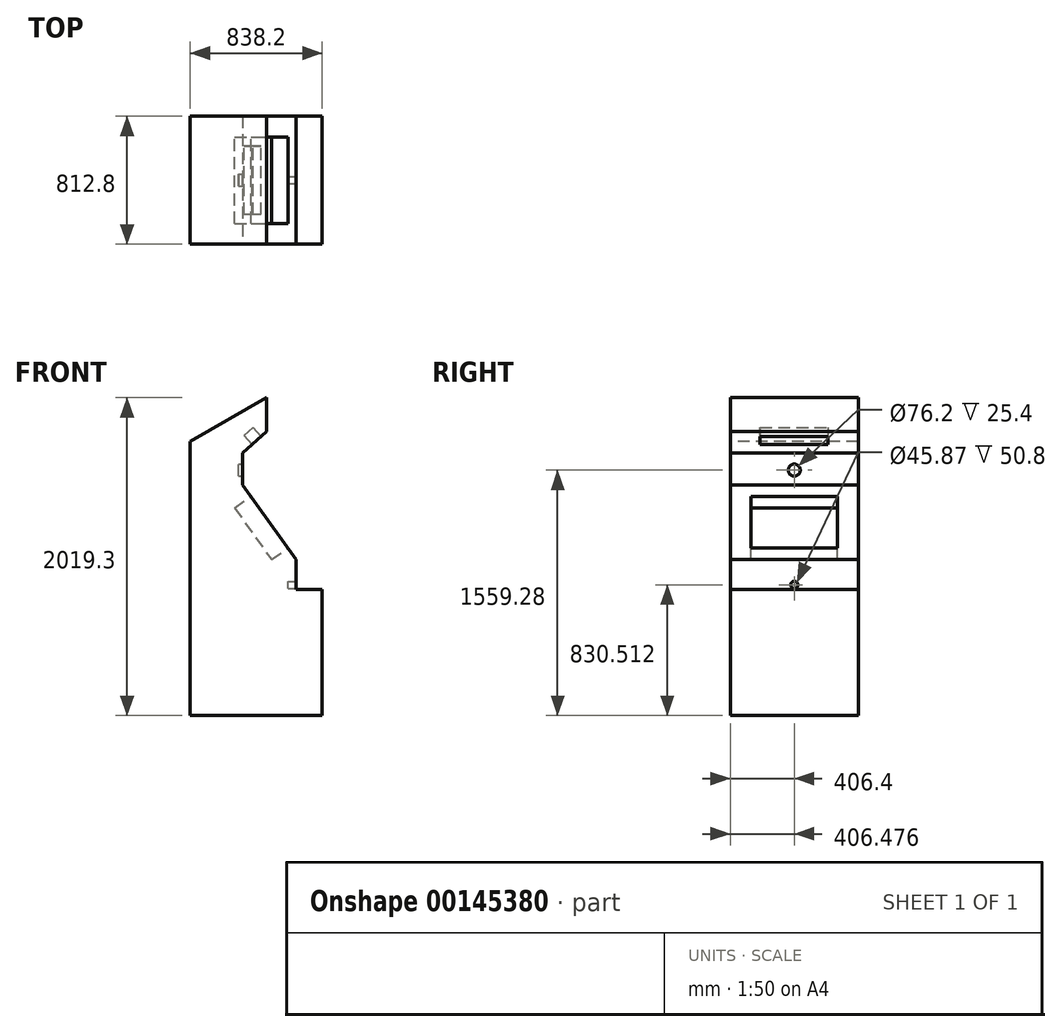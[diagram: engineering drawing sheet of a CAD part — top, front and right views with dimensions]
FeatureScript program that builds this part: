
annotation { "Feature Type Name" : "Feature", "Feature Type Description" : "" }
export const myFeature = defineFeature(function(context is Context, id is Id, definition is map)
    precondition{}
    {
        {
            var Q0;
            Q0=qCreatedBy(makeId("Front.planeOp"),FACE);
            var sketch = newSketch(context, id + "F0", { "sketchPlane" : qUnion([Q0])});
            skLineSegment(sketch, "E0", {"start": v(327.5, 1741.34) * mm, "end": v(-156.43, 1461.94) * mm});
            skLineSegment(sketch, "E1", {"start": v(-156.43, 1461.94) * mm, "end": v(-156.43, -277.96) * mm});
            skLineSegment(sketch, "E2", {"start": v(327.5, 1741.34) * mm, "end": v(327.5, 1525.44) * mm});
            skLineSegment(sketch, "E3", {"start": v(-156.43, -277.96) * mm, "end": v(681.77, -277.96) * mm});
            skLineSegment(sketch, "E4", {"start": v(681.77, -277.96) * mm, "end": v(681.77, 522.14) * mm});
            skLineSegment(sketch, "E5", {"start": v(681.77, 522.14) * mm, "end": v(516.67, 522.14) * mm});
            skLineSegment(sketch, "E6", {"start": v(516.67, 522.14) * mm, "end": v(516.67, 712.64) * mm});
            skLineSegment(sketch, "E7", {"start": v(177, 1391.13) * mm, "end": v(177, 1187.93) * mm});
            skLineSegment(sketch, "E8", {"start": v(177, 1187.93) * mm, "end": v(516.67, 712.64) * mm});
            skLineSegment(sketch, "E9", {"start": v(327.5, 1525.44) * mm, "end": v(177, 1391.13) * mm});
            skSolve(sketch);
        }
        {
            var Q0;
            Q0 = qSketchRegion(id + "F0", true);
            extrude(context, id + "F1", {"entities" : qUnion([Q0]), "oppositeDirection" : true, "depth" : 812.8 * mm});
        }
        {
            var Q0;
            Q0=makeQuery(id+"F1.opExtrude","SWEPT_FACE",FACE,{"disambiguationData":[OSD([sQuery(id+"F0.wireOp",EDGE,"E9")])]});
            var sketch = newSketch(context, id + "F2", { "sketchPlane" : qUnion([Q0])});
            skPoint(sketch, "E10", {"position": v(1259.98, -406.4) * mm});
            skLineSegment(sketch, "E11", {"start": v(1138.14, -190.1) * mm, "end": v(1138.14, -621.9) * mm});
            skLineSegment(sketch, "E12", {"start": v(1138.14, -190.1) * mm, "end": v(1214.34, -190.1) * mm});
            skLineSegment(sketch, "E13", {"start": v(1214.34, -190.1) * mm, "end": v(1214.34, -621.9) * mm});
            skLineSegment(sketch, "E14", {"start": v(1214.34, -621.9) * mm, "end": v(1138.14, -621.9) * mm});
            skSolve(sketch);
        }
        {
            var Q0;
            Q0 = qSketchRegion(id + "F2", true);
            extrude(context, id + "F3", {"entities" : qUnion([Q0]), "operationType" : NewBodyOperationType.REMOVE, "oppositeDirection" : true, "depth" : 76.2 * mm});
        }
        {
            var Q0;
            Q0=makeQuery(id+"F1.opExtrude","SWEPT_FACE",FACE,{"disambiguationData":[OSD([sQuery(id+"F0.wireOp",EDGE,"E8")])]});
            var sketch = newSketch(context, id + "F4", { "sketchPlane" : qUnion([Q0])});
            skPoint(sketch, "E15.centerSnap0", {"position": v(0, 571.47) * mm});
            skPoint(sketch, "E15.centerSnap1", {"position": v(406.4, 279.37) * mm});
            skLineSegment(sketch, "E16.bottom", {"start": v(131.78, 772.98) * mm, "end": v(681.02, 772.98) * mm});
            skLineSegment(sketch, "E16.top", {"start": v(131.78, 369.95) * mm, "end": v(681.02, 369.95) * mm});
            skLineSegment(sketch, "E16.left", {"start": v(131.78, 772.98) * mm, "end": v(131.78, 369.95) * mm});
            skLineSegment(sketch, "E16.right", {"start": v(681.02, 772.98) * mm, "end": v(681.02, 369.95) * mm});
            skPoint(sketch, "E17", {"position": v(406.4, 571.47) * mm});
            skPoint(sketch, "E17.positionSnap0", {"position": v(131.78, 571.47) * mm});
            skPoint(sketch, "E17.positionSnap1", {"position": v(406.4, 369.95) * mm});
            skSolve(sketch);
        }
        {
            var Q0;
            Q0 = qSketchRegion(id + "F4", true);
            extrude(context, id + "F5", {"entities" : qUnion([Q0]), "operationType" : NewBodyOperationType.REMOVE, "oppositeDirection" : true, "depth" : 127 * mm});
        }
        {
            var Q0;
            Q0=makeQuery(id+"F1.opExtrude","SWEPT_FACE",FACE,{"disambiguationData":[OSD([sQuery(id+"F0.wireOp",EDGE,"E7")])]});
            var sketch = newSketch(context, id + "F6", { "sketchPlane" : qUnion([Q0])});
            skCircle(sketch, "E18", {"center": v(406.4, 1281.32) * mm, "radius": 38.1 * mm});
            skPoint(sketch, "E18.centerSnap0", {"position": v(406.4, 1187.93) * mm});
            skSolve(sketch);
        }
        {
            var Q0;
            Q0 = qSketchRegion(id + "F6", true);
            extrude(context, id + "F7", {"entities" : qUnion([Q0]), "operationType" : NewBodyOperationType.REMOVE, "oppositeDirection" : true, "depth" : 25.4 * mm});
        }
        {
            var Q0;
            Q0=makeQuery(id+"F1.opExtrude","SWEPT_FACE",FACE,{"disambiguationData":[OSD([sQuery(id+"F0.wireOp",EDGE,"E6")])]});
            var sketch = newSketch(context, id + "F8", { "sketchPlane" : qUnion([Q0])});
            skPoint(sketch, "E19", {"position": v(406.48, 1277.9) * mm});
            skLineSegment(sketch, "E20", {"start": v(406.48, 1277.9) * mm, "end": v(406.48, -316.7) * mm, "construction": true});
            skLineSegment(sketch, "E21", {"start": v(406.48, 1277.9) * mm, "end": v(406.48, 1738.96) * mm, "construction": true});
            skPoint(sketch, "E22", {"position": v(406.48, 552.55) * mm});
            skCircle(sketch, "E23", {"center": v(406.48, 552.55) * mm, "radius": 22.94 * mm});
            skSolve(sketch);
        }
        {
            var Q0;
            Q0 = qSketchRegion(id + "F8", true);
            extrude(context, id + "F9", {"entities" : qUnion([Q0]), "operationType" : NewBodyOperationType.REMOVE, "oppositeDirection" : true, "depth" : 50.8 * mm});
        }
    });
